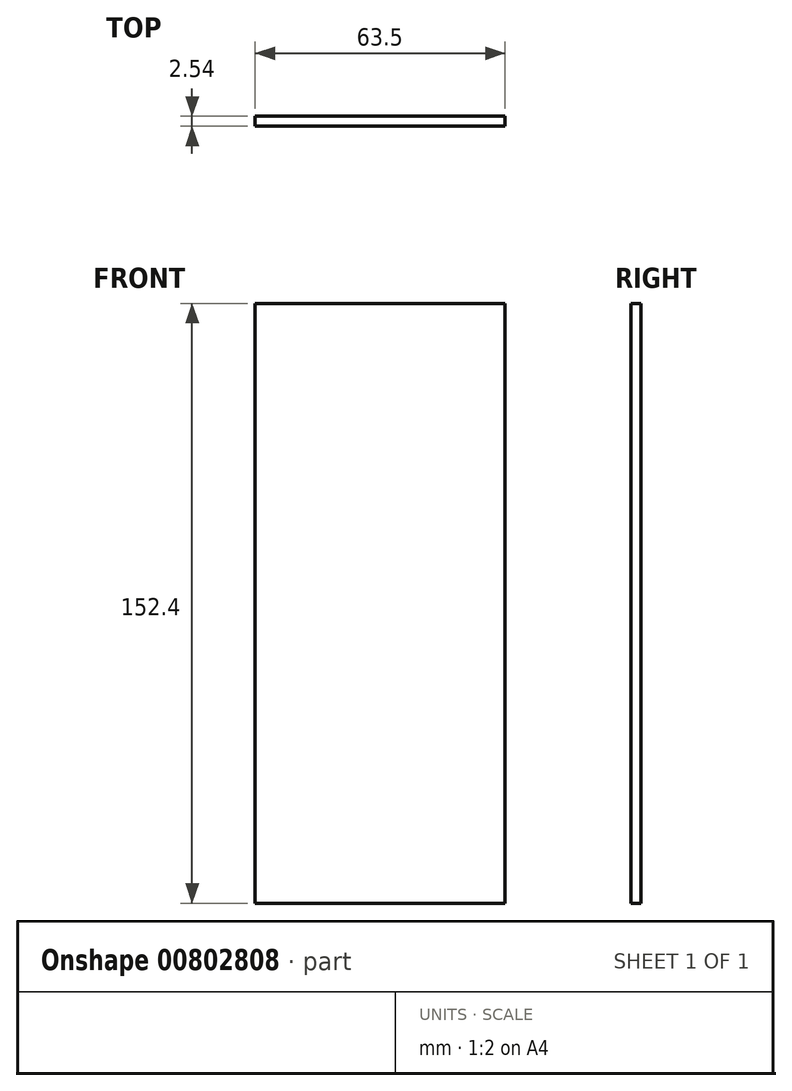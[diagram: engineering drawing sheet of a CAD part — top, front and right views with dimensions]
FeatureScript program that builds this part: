
annotation { "Feature Type Name" : "Feature", "Feature Type Description" : "" }
export const myFeature = defineFeature(function(context is Context, id is Id, definition is map)
    precondition{}
    {
        {
            var Q0;
            Q0=qCreatedBy(makeId("Front.planeOp"),FACE);
            var sketch = newSketch(context, id + "F0", { "sketchPlane" : qUnion([Q0])});
            skLineSegment(sketch, "E0.bottom", {"start": v(0, 0) * mm, "end": v(-63.5, 0) * mm});
            skLineSegment(sketch, "E0.top", {"start": v(0, 152.4) * mm, "end": v(-63.5, 152.4) * mm});
            skLineSegment(sketch, "E0.left", {"start": v(0, 0) * mm, "end": v(0, 152.4) * mm});
            skLineSegment(sketch, "E0.right", {"start": v(-63.5, 0) * mm, "end": v(-63.5, 152.4) * mm});
            skSolve(sketch);
        }
        {
            var Q0;
            Q0=makeQuery(id+"F0.imprint","IMPRINT",FACE,{"disambiguationData":[TD([[makeQuery(id+"F0.imprint","IMPRINT",EDGE,{"derivedFrom":sQuery(id+"F0.wireOp",EDGE,"E0.bottom")}),-1.0]])]});
            extrude(context, id + "F1", {"entities" : qUnion([Q0]), "depth" : 2.54 * mm, "offsetDistance" : 25.4 * mm});
        }
    });
